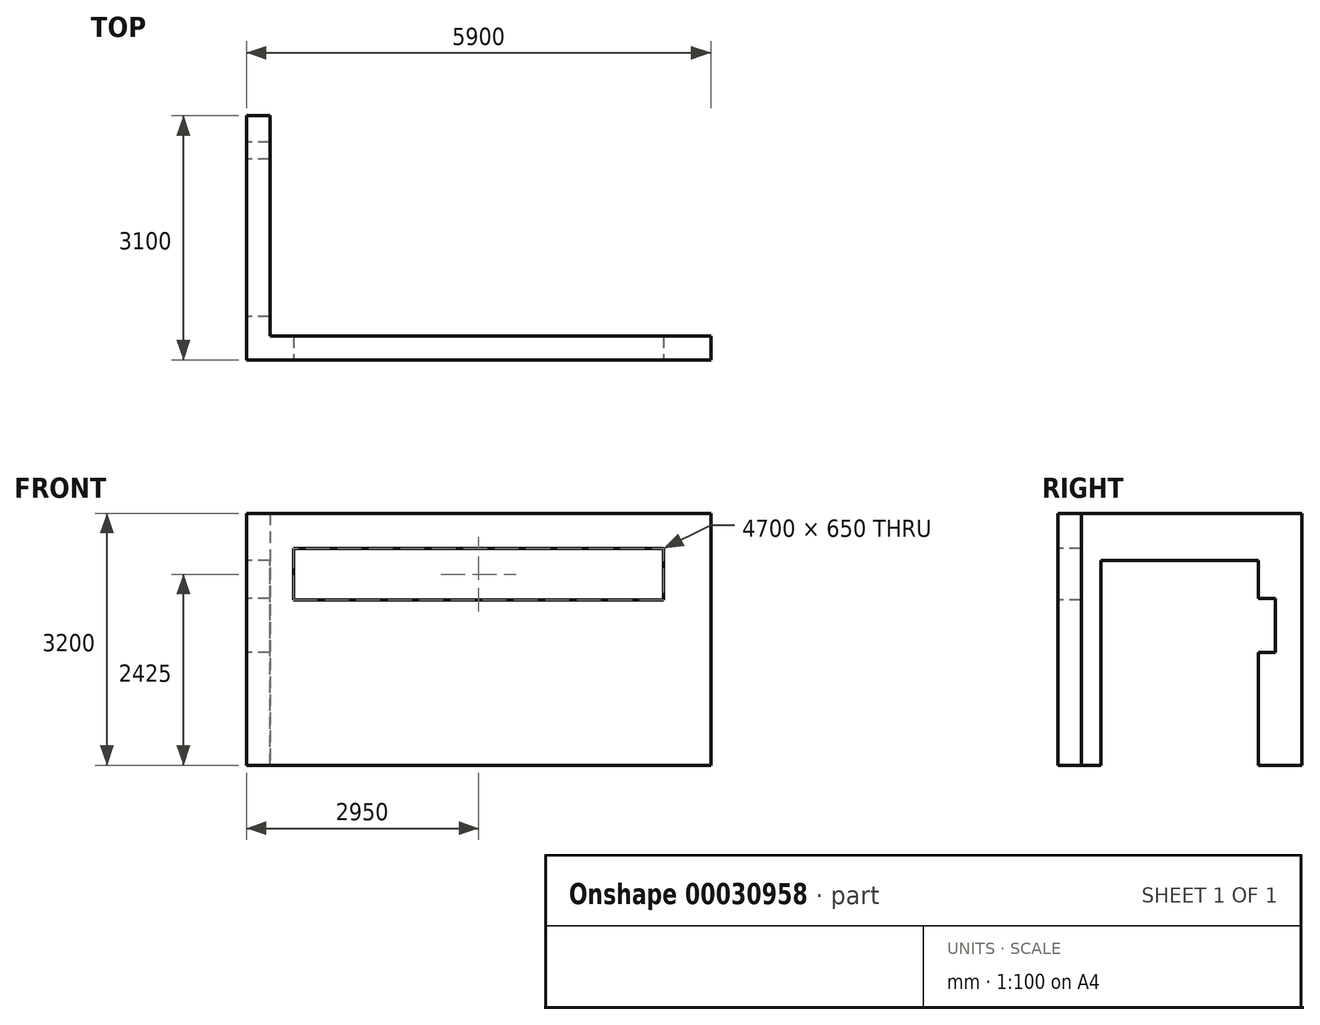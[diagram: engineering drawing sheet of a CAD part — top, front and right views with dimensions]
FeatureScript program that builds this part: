
annotation { "Feature Type Name" : "Feature", "Feature Type Description" : "" }
export const myFeature = defineFeature(function(context is Context, id is Id, definition is map)
    precondition{}
    {
        {
            var Q0;
            Q0=qCreatedBy(makeId("Top.planeOp"),FACE);
            var sketch = newSketch(context, id + "F0", { "sketchPlane" : qUnion([Q0])});
            skLineSegment(sketch, "E0", {"start": v(0, 0) * mm, "end": v(0, -300) * mm});
            skLineSegment(sketch, "E1", {"start": v(0, -300) * mm, "end": v(-5900, -300) * mm});
            skLineSegment(sketch, "E2", {"start": v(-5900, -300) * mm, "end": v(-5900, 2800) * mm});
            skLineSegment(sketch, "E3", {"start": v(-5900, 2800) * mm, "end": v(-5600, 2800) * mm});
            skLineSegment(sketch, "E4", {"start": v(-5600, 2800) * mm, "end": v(-5600, 0) * mm});
            skLineSegment(sketch, "E5", {"start": v(-5600, 0) * mm, "end": v(0, 0) * mm});
            skSolve(sketch);
        }
        {
            var Q0;
            Q0 = qSketchRegion(id + "F0", true);
            extrude(context, id + "F1", {"entities" : qUnion([Q0]), "depth" : 3200 * mm});
        }
        {
            var Q0;
            Q0=makeQuery(id+"F1.opExtrude","SWEPT_FACE",FACE,{"disambiguationData":[OSD([sQuery(id+"F0.wireOp",EDGE,"E1")])]});
            var sketch = newSketch(context, id + "F2", { "sketchPlane" : qUnion([Q0])});
            skLineSegment(sketch, "E6.bottom", {"start": v(-5300, 2750) * mm, "end": v(-600, 2750) * mm});
            skLineSegment(sketch, "E6.top", {"start": v(-5300, 2100) * mm, "end": v(-600, 2100) * mm});
            skLineSegment(sketch, "E6.left", {"start": v(-5300, 2750) * mm, "end": v(-5300, 2100) * mm});
            skLineSegment(sketch, "E6.right", {"start": v(-600, 2750) * mm, "end": v(-600, 2100) * mm});
            skSolve(sketch);
        }
        {
            var Q0;
            Q0=makeQuery(id+"F2.imprint","IMPRINT",FACE,{"disambiguationData":[TD([[makeQuery(id+"F2.imprint","IMPRINT",EDGE,{"derivedFrom":sQuery(id+"F2.wireOp",EDGE,"E6.bottom")}),-1.0]])]});
            extrude(context, id + "F3", {"entities" : qUnion([Q0]), "operationType" : NewBodyOperationType.REMOVE, "oppositeDirection" : true, "depth" : 500 * mm});
        }
        {
            var Q0;
            Q0=makeQuery(id+"F1.opExtrude","SWEPT_FACE",FACE,{"disambiguationData":[OSD([sQuery(id+"F0.wireOp",EDGE,"E2")])]});
            var sketch = newSketch(context, id + "F4", { "sketchPlane" : qUnion([Q0])});
            skLineSegment(sketch, "E7.bottom", {"start": v(-2250, 2600) * mm, "end": v(-250, 2600) * mm});
            skLineSegment(sketch, "E7.top", {"start": v(-2250, -2600) * mm, "end": v(-250, -2600) * mm});
            skLineSegment(sketch, "E7.left", {"start": v(-2250, 2600) * mm, "end": v(-2250, -2600) * mm});
            skLineSegment(sketch, "E7.right", {"start": v(-250, 2600) * mm, "end": v(-250, -2600) * mm});
            skPoint(sketch, "E7.middle", {"position": v(-1250, 0) * mm});
            skSolve(sketch);
        }
        {
            var Q0;
            Q0 = qSketchRegion(id + "F4", true);
            extrude(context, id + "F5", {"entities" : qUnion([Q0]), "operationType" : NewBodyOperationType.REMOVE, "endBound" : BoundingType.THROUGH_ALL, "oppositeDirection" : true, "depth" : 25 * mm});
        }
        {
            var Q0;
            Q0 = qSketchRegion(id + "F4", true);
            extrude(context, id + "F6", {"entities" : qUnion([Q0]), "operationType" : NewBodyOperationType.REMOVE, "oppositeDirection" : true, "depth" : 1000 * mm});
        }
        {
            var Q0;
            Q0=makeQuery(id+"F1.opExtrude","SWEPT_FACE",FACE,{"disambiguationData":[OSD([sQuery(id+"F0.wireOp",EDGE,"E2")])]});
            var sketch = newSketch(context, id + "F7", { "sketchPlane" : qUnion([Q0])});
            skLineSegment(sketch, "E8.bottom", {"start": v(-2467.3, 2120.18) * mm, "end": v(-1122.3, 2120.18) * mm});
            skLineSegment(sketch, "E8.top", {"start": v(-2467.3, 1432.13) * mm, "end": v(-1122.3, 1432.13) * mm});
            skLineSegment(sketch, "E8.left", {"start": v(-2467.3, 2120.18) * mm, "end": v(-2467.3, 1432.13) * mm});
            skLineSegment(sketch, "E8.right", {"start": v(-1122.3, 2120.18) * mm, "end": v(-1122.3, 1432.13) * mm});
            skSolve(sketch);
        }
        {
            var Q0;
            Q0 = qSketchRegion(id + "F7", true);
            extrude(context, id + "F8", {"entities" : qUnion([Q0]), "operationType" : NewBodyOperationType.REMOVE, "endBound" : BoundingType.THROUGH_ALL, "oppositeDirection" : true, "depth" : 25 * mm});
        }
    });
